# Revit family: ADB Fourneaux Electrique L1000
name_source: partatom
category: Equipement spécialisé
units: mm (PartAtom-declared; Revit-internal decimal feet)

## family parameters
Basée sur le plan de construction = Non
Conserver l'orientation des annotations = Non
Cote de connecteur circulaire = Utiliser le diamètre
Couper avec des vides une fois chargée = Non
Numéro OmniClass = 23.40.40.14.17.11
Partagée = Non
Repère de localisation dans la pièce = Non
Titre OmniClass = Cookers, Ovens, Stoves
Toujours verticalement = Oui
Type d'élément = Normal

## types (2) — shared parameters
B = 190 mm
C = 420 mm  [stored 1.37795 ft]
Commentaires du type = Gamme Ambassade - Fourneaux électriques
Fabricant = Société Industrielle de Lacanche
URL = https://www.ambassade-de-bourgogne.com
zero-valued in all types: Elévation par défaut

## per-type parameters (varying)
| type | CE 1052 P | CE 1052 VTR | Description | Modèle | Pbase | Poids net à vide | Table |
| 5 foyers radiants 2 fours - CE 1052 VTR | Non | Oui | Fourneau électrique - 5 foyers radiants 2 fours électriques | CE 1052 VTR | 16900 W | 120.00 kg | CE1051 VTR_CE 1052 VTR_5 foyers radiants |
| 5 plaques électriques 2 fours - CE 1052 P | Oui | Non | Fourneau électrique - 5 plaques électriques 2 fours électriques | CE 1052 P | 14600 W | 132.00 kg | CE1051B_CE1051E_CE1052P_5 plaques électriques |

note: [stored X ft] marks values corroborated as IEEE doubles in the binary element streams (Revit-internal decimal feet)
